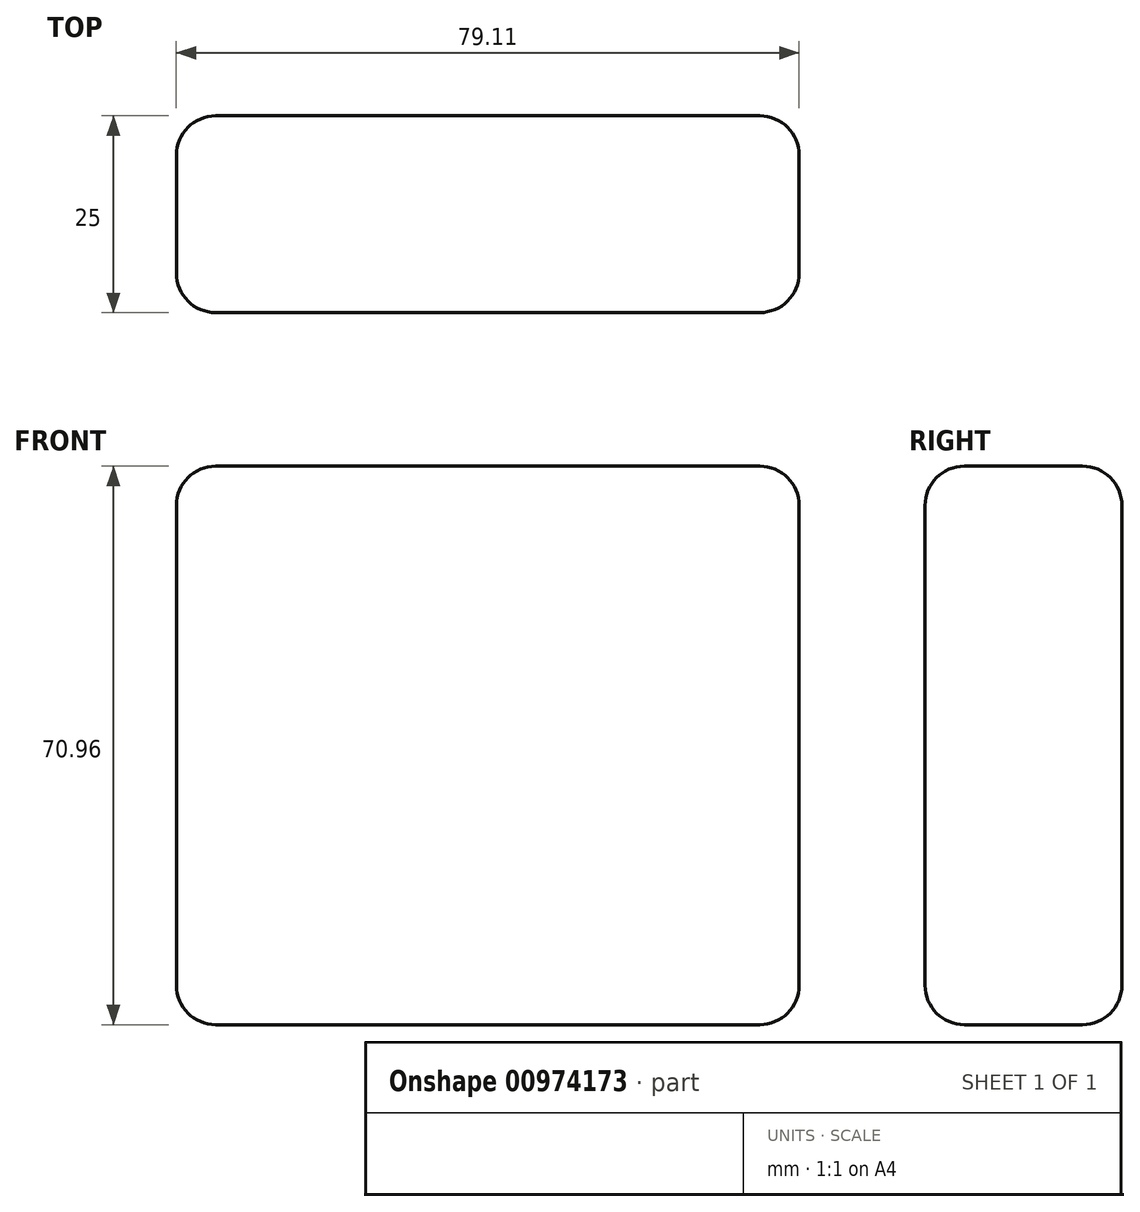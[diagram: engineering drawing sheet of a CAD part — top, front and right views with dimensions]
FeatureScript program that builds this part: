
annotation { "Feature Type Name" : "Feature", "Feature Type Description" : "" }
export const myFeature = defineFeature(function(context is Context, id is Id, definition is map)
    precondition{}
    {
        {
            var Q0;
            Q0=qCreatedBy(makeId("Front.planeOp"),FACE);
            var sketch = newSketch(context, id + "F0", { "sketchPlane" : qUnion([Q0])});
            skLineSegment(sketch, "E0.bottom", {"start": v(-87.29, 43.4) * mm, "end": v(-8.18, 43.4) * mm});
            skLineSegment(sketch, "E0.top", {"start": v(-87.29, -27.56) * mm, "end": v(-8.18, -27.56) * mm});
            skLineSegment(sketch, "E0.left", {"start": v(-87.29, 43.4) * mm, "end": v(-87.29, -27.56) * mm});
            skLineSegment(sketch, "E0.right", {"start": v(-8.18, 43.4) * mm, "end": v(-8.18, -27.56) * mm});
            skSolve(sketch);
        }
        {
            var Q0;
            Q0=makeQuery(id+"F0.imprint","IMPRINT",FACE,{"disambiguationData":[TD([[makeQuery(id+"F0.imprint","IMPRINT",EDGE,{"derivedFrom":sQuery(id+"F0.wireOp",EDGE,"E0.bottom")}),-1.0]])]});
            extrude(context, id + "F1", {"entities" : qUnion([Q0]), "depth" : 25 * mm, "offsetDistance" : 25 * mm});
        }
        {
            var Q0;
            Q0=makeQuery(id+"F1.opExtrude","SWEPT_FACE",FACE,{"disambiguationData":[OSD([sQuery(id+"F0.wireOp",EDGE,"E0.right")])]});
            var Q1;
            Q1=makeQuery(id+"F1.opExtrude","SWEPT_FACE",FACE,{"disambiguationData":[OSD([sQuery(id+"F0.wireOp",EDGE,"E0.left")])]});
            var Q2;
            Q2=makeQuery(id+"F1.opExtrude","SWEPT_FACE",FACE,{"disambiguationData":[OSD([sQuery(id+"F0.wireOp",EDGE,"E0.bottom")])]});
            var Q3;
            Q3=makeQuery(id+"F1.opExtrude","SWEPT_FACE",FACE,{"disambiguationData":[OSD([sQuery(id+"F0.wireOp",EDGE,"E0.top")])]});
            fillet(context, id + "F2", {"entities" : qUnion([Q0, Q1, Q2, Q3]), "radius" : 5 * mm, "tangentPropagation" : true, "allowEdgeOverflow" : false});
        }
    });
